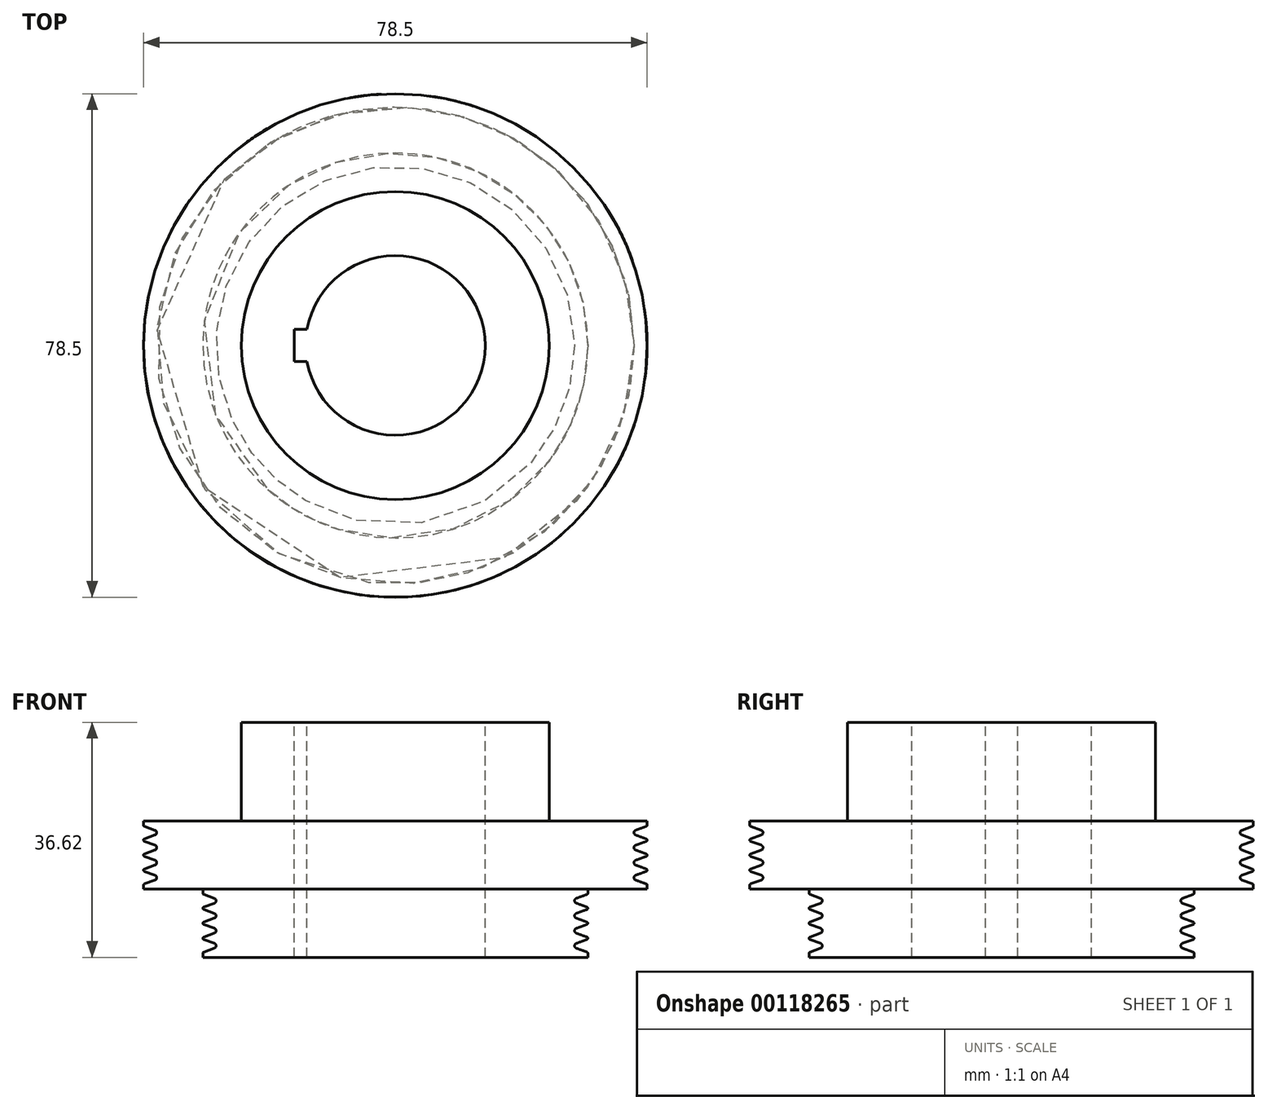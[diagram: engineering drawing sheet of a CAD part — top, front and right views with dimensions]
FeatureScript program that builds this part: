
annotation { "Feature Type Name" : "Feature", "Feature Type Description" : "" }
export const myFeature = defineFeature(function(context is Context, id is Id, definition is map)
    precondition{}
    {
        {
            var Q0;
            Q0=qCreatedBy(makeId("Front.planeOp"),FACE);
            var sketch = newSketch(context, id + "F0", { "sketchPlane" : qUnion([Q0])});
            skLineSegment(sketch, "E0", {"start": v(0, 0) * mm, "end": v(-14, 0) * mm, "construction": true});
            skLineSegment(sketch, "E1", {"start": v(-14, 0) * mm, "end": v(-39.25, 0) * mm});
            skLineSegment(sketch, "E2", {"start": v(-39.25, 1.8) * mm, "end": v(-39.25, 0.63) * mm, "construction": true});
            skLineSegment(sketch, "E3", {"start": v(-39.25, 1.8) * mm, "end": v(-37.59, 1.8) * mm, "construction": true});
            skArc(sketch, "E4", {"start": v(-37.45, 1.42) * mm, "mid": v(-37.19, 1.8) * mm, "end": v(-37.45, 2.18) * mm});
            skLineSegment(sketch, "E5", {"start": v(-39.25, 0.63) * mm, "end": v(-39.05, 0.63) * mm, "construction": true});
            skArc(sketch, "E6", {"start": v(-39.12, 0.82) * mm, "mid": v(-39.21, 0.74) * mm, "end": v(-39.25, 0.63) * mm});
            skLineSegment(sketch, "E7", {"start": v(-39.12, 0.82) * mm, "end": v(-37.45, 1.42) * mm});
            skLineSegment(sketch, "E8", {"start": v(-37.59, 1.8) * mm, "end": v(-37.19, 1.8) * mm, "construction": true});
            skLineSegment(sketch, "E9.MirrorCS", {"start": v(-39.12, 2.78) * mm, "end": v(-37.45, 2.18) * mm});
            skArc(sketch, "E10.MirrorC", {"start": v(-39.12, 2.78) * mm, "mid": v(-39.25, 2.97) * mm, "end": v(-39.12, 3.16) * mm});
            skLineSegment(sketch, "E11", {"start": v(-39.25, 1.8) * mm, "end": v(-39.25, 10.62) * mm, "construction": true});
            skLineSegment(sketch, "E12", {"start": v(-39.25, 0.63) * mm, "end": v(-39.25, 0) * mm});
            skLineSegment(sketch, "E13", {"start": v(-39.25, 2.97) * mm, "end": v(-39.05, 2.97) * mm, "construction": true});
            skLineSegment(sketch, "E14.MirrorCS", {"start": v(-39.12, 5.12) * mm, "end": v(-37.45, 4.52) * mm});
            skLineSegment(sketch, "E15.MirrorCS", {"start": v(-39.12, 3.16) * mm, "end": v(-37.45, 3.76) * mm});
            skArc(sketch, "E16.MirrorCS", {"start": v(-37.45, 4.52) * mm, "mid": v(-37.19, 4.14) * mm, "end": v(-37.45, 3.76) * mm});
            skArc(sketch, "E17.MirrorC", {"start": v(-39.12, 3.16) * mm, "mid": v(-39.25, 2.97) * mm, "end": v(-39.12, 2.78) * mm});
            skLineSegment(sketch, "E18", {"start": v(-39.25, 4.14) * mm, "end": v(-37.19, 4.14) * mm});
            skArc(sketch, "E19.MirrorC", {"start": v(-39.12, 5.12) * mm, "mid": v(-39.25, 5.3) * mm, "end": v(-39.12, 5.5) * mm});
            skLineSegment(sketch, "E20", {"start": v(-39.25, 5.3) * mm, "end": v(-39.05, 5.3) * mm, "construction": true});
            skLineSegment(sketch, "E21.MirrorCS", {"start": v(-39.12, 5.5) * mm, "end": v(-37.45, 6.1) * mm});
            skArc(sketch, "E22.MirrorCS", {"start": v(-37.45, 6.1) * mm, "mid": v(-37.19, 6.48) * mm, "end": v(-37.45, 6.86) * mm});
            skLineSegment(sketch, "E23.MirrorCS", {"start": v(-39.12, 7.46) * mm, "end": v(-37.45, 6.86) * mm});
            skArc(sketch, "E24.MirrorCS", {"start": v(-39.12, 7.84) * mm, "mid": v(-39.25, 7.65) * mm, "end": v(-39.12, 7.46) * mm});
            skLineSegment(sketch, "E25.MirrorCS", {"start": v(-39.12, 7.84) * mm, "end": v(-37.45, 8.44) * mm});
            skArc(sketch, "E26.MirrorCS", {"start": v(-37.45, 9.2) * mm, "mid": v(-37.19, 8.82) * mm, "end": v(-37.45, 8.44) * mm});
            skLineSegment(sketch, "E27.MirrorCS", {"start": v(-39.12, 9.8) * mm, "end": v(-37.45, 9.2) * mm});
            skArc(sketch, "E28.MirrorCS", {"start": v(-39.12, 9.8) * mm, "mid": v(-39.21, 9.87) * mm, "end": v(-39.25, 9.99) * mm});
            skLineSegment(sketch, "E29.MirrorCS", {"start": v(-39.25, 9.99) * mm, "end": v(-39.25, 10.62) * mm});
            skLineSegment(sketch, "E30.MirrorCS", {"start": v(-14, 10.62) * mm, "end": v(-39.25, 10.62) * mm});
            skLineSegment(sketch, "E31.MirrorCS", {"start": v(0, 10.62) * mm, "end": v(-14, 10.62) * mm, "construction": true});
            skLineSegment(sketch, "E32", {"start": v(-14, 10.62) * mm, "end": v(-14, 0) * mm});
            skLineSegment(sketch, "E33", {"start": v(0, 10.62) * mm, "end": v(0, 0) * mm, "construction": true});
            skArc(sketch, "E34", {"start": v(-28.2, -2.18) * mm, "mid": v(-27.94, -1.8) * mm, "end": v(-28.2, -1.42) * mm});
            skArc(sketch, "E35", {"start": v(-30, -0.63) * mm, "mid": v(-29.96, -0.74) * mm, "end": v(-29.87, -0.82) * mm});
            skLineSegment(sketch, "E36", {"start": v(-29.87, -0.82) * mm, "end": v(-28.2, -1.42) * mm});
            skLineSegment(sketch, "E37", {"start": v(-30, -0.63) * mm, "end": v(-30, 0) * mm});
            skLineSegment(sketch, "E38", {"start": v(-30.57, -1.8) * mm, "end": v(-25.09, -1.8) * mm, "construction": true});
            skLineSegment(sketch, "E39.MirrorCS", {"start": v(-29.87, -2.78) * mm, "end": v(-28.2, -2.18) * mm});
            skArc(sketch, "E40.MirrorC", {"start": v(-29.87, -3.16) * mm, "mid": v(-30, -2.97) * mm, "end": v(-29.87, -2.78) * mm});
            skLineSegment(sketch, "E41", {"start": v(-30.6, -2.97) * mm, "end": v(-25.04, -2.97) * mm, "construction": true});
            skArc(sketch, "E42.MirrorC", {"start": v(-29.87, -5.5) * mm, "mid": v(-30, -5.31) * mm, "end": v(-29.87, -5.12) * mm});
            skArc(sketch, "E43.MirrorC", {"start": v(-28.2, -3.76) * mm, "mid": v(-27.94, -4.14) * mm, "end": v(-28.2, -4.52) * mm});
            skLineSegment(sketch, "E44.MirrorCS", {"start": v(-29.87, -3.16) * mm, "end": v(-28.2, -3.76) * mm});
            skLineSegment(sketch, "E45.MirrorCS", {"start": v(-29.87, -5.12) * mm, "end": v(-28.2, -4.52) * mm});
            skLineSegment(sketch, "E46", {"start": v(-30.93, -5.31) * mm, "end": v(-25.12, -5.31) * mm, "construction": true});
            skLineSegment(sketch, "E47.MirrorCS", {"start": v(-29.87, -5.5) * mm, "end": v(-28.2, -6.1) * mm});
            skArc(sketch, "E48.MirrorC", {"start": v(-28.2, -6.86) * mm, "mid": v(-27.94, -6.48) * mm, "end": v(-28.2, -6.1) * mm});
            skLineSegment(sketch, "E49.MirrorCS", {"start": v(-29.87, -7.46) * mm, "end": v(-28.2, -6.86) * mm});
            skArc(sketch, "E50.MirrorC", {"start": v(-29.87, -7.46) * mm, "mid": v(-30, -7.65) * mm, "end": v(-29.87, -7.84) * mm});
            skLineSegment(sketch, "E51.MirrorCS", {"start": v(-29.87, -7.84) * mm, "end": v(-28.2, -8.44) * mm});
            skArc(sketch, "E52.MirrorC", {"start": v(-28.2, -8.44) * mm, "mid": v(-27.94, -8.82) * mm, "end": v(-28.2, -9.2) * mm});
            skLineSegment(sketch, "E53.MirrorCS", {"start": v(-29.87, -9.8) * mm, "end": v(-28.2, -9.2) * mm});
            skArc(sketch, "E54.MirrorC", {"start": v(-30, -10) * mm, "mid": v(-29.96, -9.88) * mm, "end": v(-29.87, -9.8) * mm});
            skLineSegment(sketch, "E55.MirrorCS", {"start": v(-30, -10) * mm, "end": v(-30, -10.62) * mm});
            skLineSegment(sketch, "E56", {"start": v(0, -10.62) * mm, "end": v(0, 0) * mm, "construction": true});
            skLineSegment(sketch, "E57", {"start": v(-14, 0) * mm, "end": v(-14, -10.62) * mm});
            skLineSegment(sketch, "E58", {"start": v(-30, -10.62) * mm, "end": v(-14, -10.62) * mm});
            skLineSegment(sketch, "E59", {"start": v(0, 10.62) * mm, "end": v(0, 26) * mm});
            skLineSegment(sketch, "E60", {"start": v(0, 26) * mm, "end": v(-14, 26) * mm, "construction": true});
            skLineSegment(sketch, "E61", {"start": v(-14, 26) * mm, "end": v(-24, 26) * mm});
            skLineSegment(sketch, "E62", {"start": v(-24, 26) * mm, "end": v(-24, 10.62) * mm});
            skLineSegment(sketch, "E63", {"start": v(-14, 26) * mm, "end": v(-14, 10.62) * mm});
            skLineSegment(sketch, "E64", {"start": v(-14, -10.62) * mm, "end": v(0, -10.62) * mm, "construction": true});
            skSolve(sketch);
        }
        {
            var Q0;
            Q0=makeQuery(id+"F0.imprint","IMPRINT",FACE,{"disambiguationData":[TD([[makeQuery(id+"F0.imprint","IMPRINT",EDGE,{"derivedFrom":sQuery(id+"F0.wireOp",EDGE,"E1")}),-1.0]])]});
            var Q1;
            Q1=makeQuery(id+"F0.imprint","IMPRINT",FACE,{"disambiguationData":[TD([[makeQuery(id+"F0.imprint","IMPRINT",EDGE,{"derivedFrom":sQuery(id+"F0.wireOp",EDGE,"E61")}),1.0]])]});
            var Q2;
            Q2=makeQuery(id+"F0.imprint","IMPRINT",FACE,{"disambiguationData":[TD([[makeQuery(id+"F0.imprint","IMPRINT",EDGE,{"derivedFrom":sQuery(id+"F0.wireOp",EDGE,"E34")}),-1.0]])]});
            var Q3;
            {var subQ2=sQuery(id+"F0.wireOp",EDGE,"DEbglehD-8Eaz-XNJQ-gYdY-BHVsD9lRFY5u");Q3=makeQuery(id+"F0.imprint","IMPRINT",FACE,{"disambiguationData":[TD([[makeQuery(id+"F0.imprint","IMPRINT",EDGE,{"derivedFrom":subQ2}),-1.0]])]});}
            var Q4;
            Q4=sQuery(id+"F0.wireOp",EDGE,"E33");
            revolve(context, id + "F1", {"entities" : qUnion([Q0, Q1, Q2, Q3]), "axis" : qUnion([Q4]), "revolveType" : RevolveType.FULL});
        }
        {
            var Q0;
            Q0=makeQuery(id+"F1.opRevolve","SWEPT_FACE",FACE,{"disambiguationData":[OSD([sQuery(id+"F0.wireOp",EDGE,"E61")])]});
            var sketch = newSketch(context, id + "F2", { "sketchPlane" : qUnion([Q0])});
            skCircle(sketch, "E65.0", {"center": v(0, 0) * mm, "radius": 14 * mm});
            skLineSegment(sketch, "E66", {"start": v(0, 0) * mm, "end": v(-14, 0) * mm, "construction": true});
            skLineSegment(sketch, "E67", {"start": v(-14, 0) * mm, "end": v(-15.75, 0) * mm});
            skLineSegment(sketch, "E68", {"start": v(-15.75, 0) * mm, "end": v(-15.75, 2.5) * mm});
            skLineSegment(sketch, "E69", {"start": v(-15.75, 2.5) * mm, "end": v(-13.77, 2.5) * mm});
            skLineSegment(sketch, "E70.MirrorCS", {"start": v(-15.75, -2.5) * mm, "end": v(-13.77, -2.5) * mm});
            skLineSegment(sketch, "E71.MirrorCS", {"start": v(-15.75, 0) * mm, "end": v(-15.75, -2.5) * mm});
            skLineSegment(sketch, "E72.1", {"start": v(-14, 0) * mm, "end": v(-39.25, 0) * mm});
            skSolve(sketch);
        }
        {
            var Q0;
            {var subQ0=sQuery(id+"F2.wireOp",EDGE,"E70.MirrorCS");Q0=makeQuery(id+"F2.imprint","IMPRINT",FACE,{"disambiguationData":[TD([[makeQuery(id+"F2.imprint","IMPRINT",EDGE,{"derivedFrom":subQ0}),1.0]])]});}
            var Q1;
            {var subQ4=sQuery(id+"F2.wireOp",EDGE,"E68");Q1=makeQuery(id+"F2.imprint","IMPRINT",FACE,{"disambiguationData":[TD([[makeQuery(id+"F2.imprint","IMPRINT",EDGE,{"derivedFrom":subQ4}),-1.0]])]});}
            var Q2;
            Q2=makeQuery(id+"F1.opRevolve","SWEPT_FACE",FACE,{"disambiguationData":[OSD([sQuery(id+"F0.wireOp",EDGE,"E58")])]});
            extrude(context, id + "F3", {"entities" : qUnion([Q0, Q1]), "operationType" : NewBodyOperationType.REMOVE, "endBound" : BoundingType.UP_TO_SURFACE, "oppositeDirection" : true, "endBoundEntityFace" : qUnion([Q2]), "depth" : 23 * mm});
        }
    });
